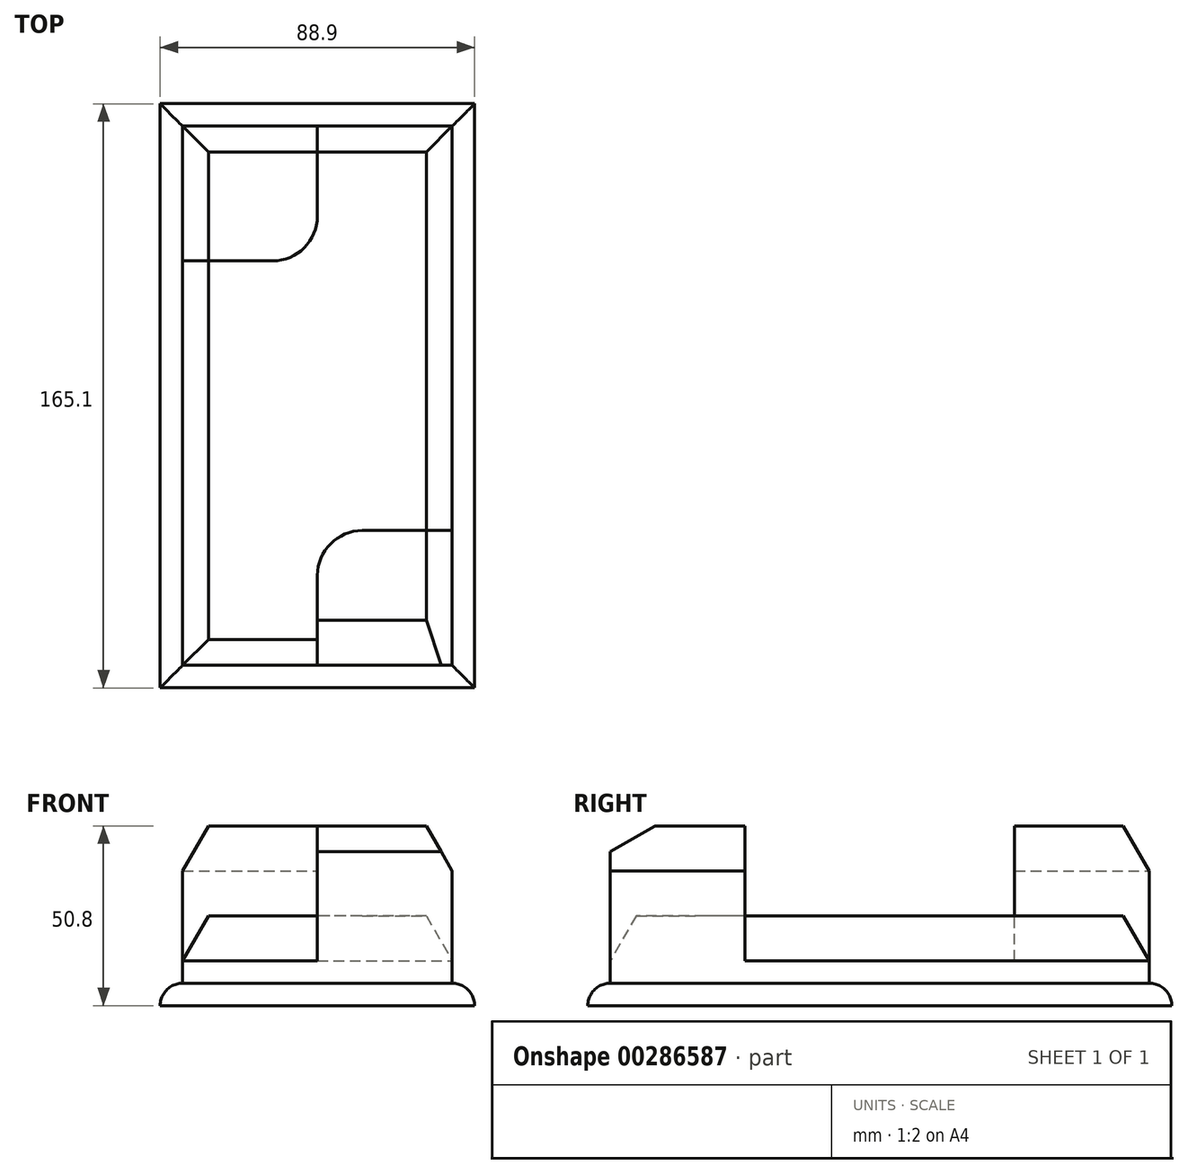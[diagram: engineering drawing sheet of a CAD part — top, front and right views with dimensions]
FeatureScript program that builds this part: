
annotation { "Feature Type Name" : "Feature", "Feature Type Description" : "" }
export const myFeature = defineFeature(function(context is Context, id is Id, definition is map)
    precondition{}
    {
        {
            var Q0;
            Q0=qCreatedBy(makeId("Top.planeOp"),FACE);
            var sketch = newSketch(context, id + "F0", { "sketchPlane" : qUnion([Q0])});
            skLineSegment(sketch, "E0.bottom", {"start": v(-52.16, 65.2) * mm, "end": v(36.74, 65.2) * mm});
            skLineSegment(sketch, "E0.top", {"start": v(-52.16, -99.9) * mm, "end": v(36.74, -99.9) * mm});
            skLineSegment(sketch, "E0.left", {"start": v(-52.16, 65.2) * mm, "end": v(-52.16, -99.9) * mm});
            skLineSegment(sketch, "E0.right", {"start": v(36.74, 65.2) * mm, "end": v(36.74, -99.9) * mm});
            skLineSegment(sketch, "E1.bottom", {"start": v(-45.8, 58.85) * mm, "end": v(30.4, 58.85) * mm});
            skLineSegment(sketch, "E1.top", {"start": v(-45.8, -93.55) * mm, "end": v(30.4, -93.55) * mm});
            skLineSegment(sketch, "E1.left", {"start": v(-45.8, 58.85) * mm, "end": v(-45.8, -93.55) * mm});
            skLineSegment(sketch, "E1.right", {"start": v(30.4, 58.85) * mm, "end": v(30.4, -93.55) * mm});
            skLineSegment(sketch, "E2", {"start": v(-7.7, 58.85) * mm, "end": v(-7.7, 33.45) * mm});
            skLineSegment(sketch, "E3", {"start": v(-20.4, 20.75) * mm, "end": v(-45.8, 20.75) * mm});
            skArc(sketch, "E4", {"start": v(-20.4, 20.75) * mm, "mid": v(-11.43, 24.47) * mm, "end": v(-7.7, 33.45) * mm});
            skLineSegment(sketch, "E5", {"start": v(-7.7, -93.55) * mm, "end": v(-7.7, -68.15) * mm});
            skPoint(sketch, "E5.startSnap0", {"position": v(-7.7, -99.9) * mm});
            skLineSegment(sketch, "E6", {"start": v(5, -55.45) * mm, "end": v(30.4, -55.45) * mm});
            skArc(sketch, "E7", {"start": v(5, -55.45) * mm, "mid": v(-3.99, -59.17) * mm, "end": v(-7.7, -68.15) * mm});
            skSolve(sketch);
        }
        {
            var Q0;
            {var subQ9=sQuery(id+"F0.wireOp",EDGE,"E2");Q0=makeQuery(id+"F0.imprint","IMPRINT",FACE,{"disambiguationData":[TD([[makeQuery(id+"F0.imprint","IMPRINT",EDGE,{"derivedFrom":subQ9}),1.0]])]});}
            extrude(context, id + "F1", {"entities" : qUnion([Q0]), "depth" : 25.4 * mm});
        }
        {
            var Q0;
            {var subQ0=sQuery(id+"F0.wireOp",EDGE,"E2");Q0=makeQuery(id+"F0.imprint","IMPRINT",FACE,{"disambiguationData":[TD([[makeQuery(id+"F0.imprint","IMPRINT",EDGE,{"derivedFrom":subQ0}),-1.0]])]});}
            var Q1;
            {var subQ0=sQuery(id+"F0.wireOp",EDGE,"E5");Q1=makeQuery(id+"F0.imprint","IMPRINT",FACE,{"disambiguationData":[TD([[makeQuery(id+"F0.imprint","IMPRINT",EDGE,{"derivedFrom":subQ0}),-1.0]])]});}
            extrude(context, id + "F2", {"entities" : qUnion([Q0, Q1]), "operationType" : NewBodyOperationType.ADD, "depth" : 50.8 * mm});
        }
        {
            var Q0;
            Q0=makeQuery(id+"F0.imprint","IMPRINT",FACE,{"disambiguationData":[TD([[makeQuery(id+"F0.imprint","IMPRINT",EDGE,{"derivedFrom":sQuery(id+"F0.wireOp",EDGE,"E0.bottom")}),-1.0]])]});
            extrude(context, id + "F3", {"entities" : qUnion([Q0]), "operationType" : NewBodyOperationType.ADD, "depth" : 6.35 * mm});
        }
        {
            var Q0;
            Q0=makeQuery(id+"F3.opExtrude","CAP_EDGE",EDGE,{"disambiguationData":[OSD([sQuery(id+"F0.wireOp",EDGE,"E0.top")])],"isStart":false});
            var Q1;
            Q1=makeQuery(id+"F3.opExtrude","CAP_EDGE",EDGE,{"disambiguationData":[OSD([sQuery(id+"F0.wireOp",EDGE,"E0.left")])],"isStart":false});
            var Q2;
            Q2=makeQuery(id+"F3.opExtrude","CAP_EDGE",EDGE,{"disambiguationData":[OSD([sQuery(id+"F0.wireOp",EDGE,"E0.right")])],"isStart":false});
            var Q3;
            Q3=makeQuery(id+"F3.opExtrude","CAP_EDGE",EDGE,{"disambiguationData":[OSD([sQuery(id+"F0.wireOp",EDGE,"E0.bottom")])],"isStart":false});
            fillet(context, id + "F4", {"entities" : qUnion([Q0, Q1, Q2, Q3]), "radius" : 6.35 * mm, "tangentPropagation" : true, "allowEdgeOverflow" : false});
        }
        {
            var Q0;
            Q0=makeQuery(id+"F1.opExtrude","CAP_EDGE",EDGE,{"disambiguationData":[OSD([sQuery(id+"F0.wireOp",EDGE,"E1.right")])],"isStart":false});
            var Q1;
            Q1=makeQuery(id+"F1.opExtrude","CAP_EDGE",EDGE,{"disambiguationData":[OSD([sQuery(id+"F0.wireOp",EDGE,"E1.bottom")])],"isStart":false});
            var Q2;
            Q2=makeQuery(id+"F1.opExtrude","CAP_EDGE",EDGE,{"disambiguationData":[OSD([sQuery(id+"F0.wireOp",EDGE,"E1.left")])],"isStart":false});
            var Q3;
            Q3=makeQuery(id+"F1.opExtrude","CAP_EDGE",EDGE,{"disambiguationData":[OSD([sQuery(id+"F0.wireOp",EDGE,"E1.top")])],"isStart":false});
            chamfer(context, id + "F5", {"entities" : qUnion([Q0, Q1, Q2, Q3]), "chamferType" : ChamferType.OFFSET_ANGLE, "width" : 12.7 * mm, "oppositeDirection" : false, "angle" : 30 * degree, "tangentPropagation" : true});
        }
        {
            var Q0;
            Q0=makeQuery(id+"F2.opExtrude","CAP_EDGE",EDGE,{"disambiguationData":[OSD([sQuery(id+"F0.wireOp",EDGE,"E1.bottom")])],"isStart":false});
            var Q1;
            Q1=makeQuery(id+"F2.opExtrude","CAP_EDGE",EDGE,{"disambiguationData":[OSD([sQuery(id+"F0.wireOp",EDGE,"E1.left")])],"isStart":false});
            var Q2;
            Q2=makeQuery(id+"F2.opExtrude","CAP_EDGE",EDGE,{"disambiguationData":[OSD([sQuery(id+"F0.wireOp",EDGE,"E1.right")])],"isStart":false});
            var Q3;
            Q3=makeQuery(id+"F2.opExtrude","CAP_EDGE",EDGE,{"disambiguationData":[OSD([sQuery(id+"F0.wireOp",EDGE,"E1.top")])],"isStart":false});
            chamfer(context, id + "F6", {"entities" : qUnion([Q0, Q1, Q2, Q3]), "chamferType" : ChamferType.OFFSET_ANGLE, "width" : 12.7 * mm, "oppositeDirection" : false, "angle" : 30 * degree, "tangentPropagation" : true});
        }
    });
